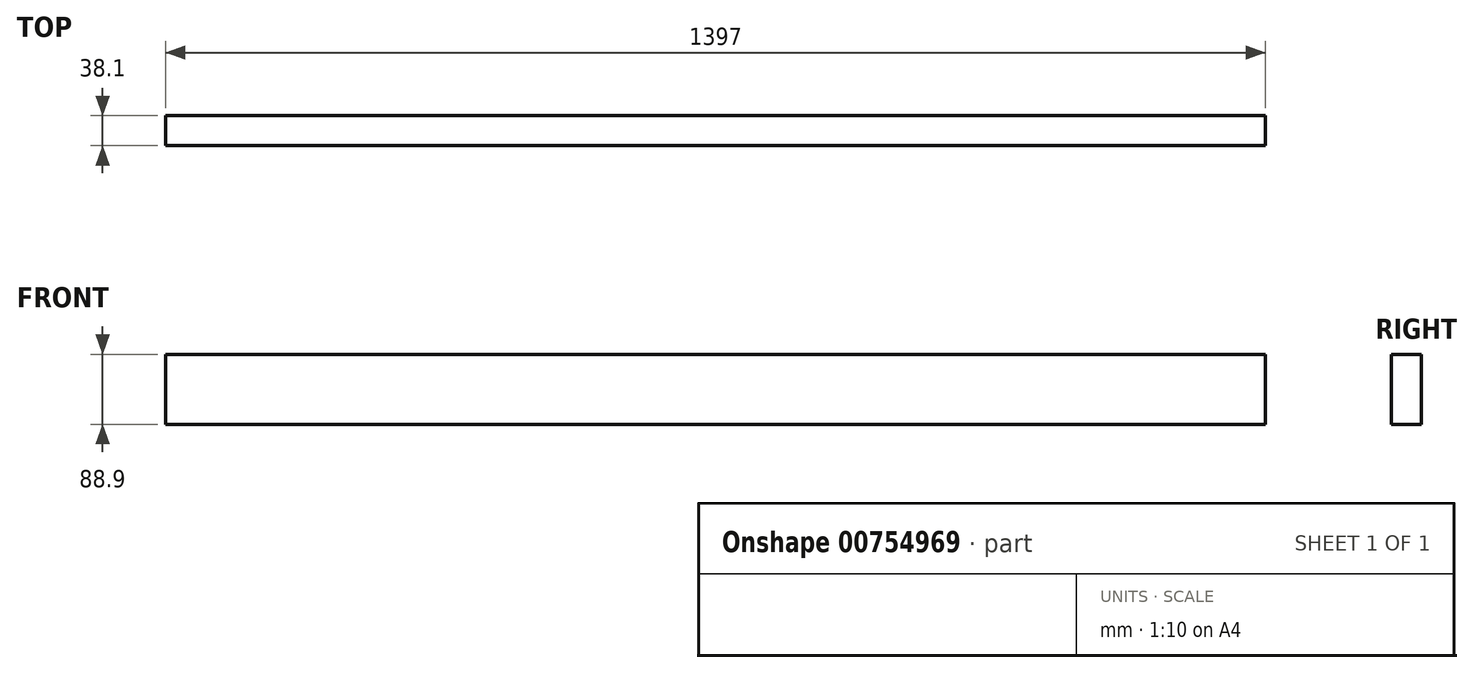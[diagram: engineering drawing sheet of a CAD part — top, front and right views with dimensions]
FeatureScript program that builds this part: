
annotation { "Feature Type Name" : "Feature", "Feature Type Description" : "" }
export const myFeature = defineFeature(function(context is Context, id is Id, definition is map)
    precondition{}
    {
        {
            var Q0;
            Q0=qCreatedBy(makeId("Right.planeOp"),FACE);
            var sketch = newSketch(context, id + "F0", { "sketchPlane" : qUnion([Q0])});
            skLineSegment(sketch, "E0.bottom", {"start": v(0, 0) * mm, "end": v(38.1, 0) * mm});
            skLineSegment(sketch, "E0.top", {"start": v(0, 88.9) * mm, "end": v(38.1, 88.9) * mm});
            skLineSegment(sketch, "E0.left", {"start": v(0, 0) * mm, "end": v(0, 88.9) * mm});
            skLineSegment(sketch, "E0.right", {"start": v(38.1, 0) * mm, "end": v(38.1, 88.9) * mm});
            skSolve(sketch);
        }
        {
            var Q0;
            Q0=makeQuery(id+"F0.imprint","IMPRINT",FACE,{"disambiguationData":[TD([[makeQuery(id+"F0.imprint","IMPRINT",EDGE,{"derivedFrom":sQuery(id+"F0.wireOp",EDGE,"E0.bottom")}),1.0]])]});
            extrude(context, id + "F1", {"entities" : qUnion([Q0]), "depth" : 1397 * mm, "offsetDistance" : 25.4 * mm});
        }
    });
